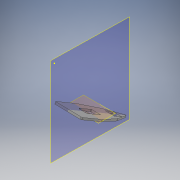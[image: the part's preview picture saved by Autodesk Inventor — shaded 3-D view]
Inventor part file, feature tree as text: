
AUTODESK INVENTOR PART (.ipt)
format: ipt  version: 2018 (Build 220112000, 112)  size: 513,024 bytes
history: native  units: mm
features: other x7, sketch x4, sheet_metal_op x3, hole x2, plane x1, fillet x1, reference x1
ambient origin geometry x8: Origin, YZ Plane, XZ Plane, XY Plane, X Axis, Y Axis, Z Axis, Center Point
bodies: Solid1 (feature_tree)
feature tree (19):
  plane  "Work Plane1"
  sheet_metal_op  "Face1"
  other  "midtplan"
  sketch  "Sketch2"  dims[d1=44.0mm d3=24.0mm d4=38.0mm d5=24.0mm d7=28.0mm d8=2.0mm]
  hole  "Hole1"  [1 undecoded]
  hole  "Hole2"  [1 undecoded]
  sheet_metal_op  "Fold1"
  fillet  "Fillet1"  Radius=2.0mm
  sheet_metal_op  "Fold2"
  sketch  "Sketch1"  dims[d0=8.0mm]
  other  "Plate1"
  reference  "Reference38"
  sketch  "Sketch3"  dims[d9=41.0mm d10=24.0mm d11=38.0mm d12=24.0mm d13=26.0mm d14=2.0mm d22=130.0mm]
  sketch  "Sketch4"  dims[d23=40.5mm d24=38.0mm d25=2.0mm d28=3.0mm d29=8.0mm d30=4.0mm d31=16.0mm d32=8.0mm d33=30.0deg d34=8.0mm d37=0.0mm d38=3.0mm d39=8.0mm d40=6.0mm d41=4.0mm d42=2.0mm d43=90.0deg d44=8.0mm d45=20.594885mm d46=0.0mm d47=3.0mm d48=8.0mm d49=6.0mm d50=4.0mm d51=2.0mm d52=90.0deg d53=8.0mm d54=20.594885mm d55=1.0mm d56=0.0mm d57=20.0mm d58=8.0mm d59=4.0mm d60=16.0mm d61=8.0mm d62=30.0deg d63=8.0mm]
  parser-record x1  (decoder bookkeeping rows leaked as tree rows — omitted from the tree; the rows remain in map.json)
  other  "modul top.iam"
  other  "vange top:1"
  other  "Definition1"
  other  "plade:1"
note: 2 required parameter values undecoded (feature->parameter linkage not recoverable at this tier; creation-order binding heuristic only, values carry confidence <= 0.55)
note: 1 file-system path scrubbed to <path> (originals preserved in map.json)
